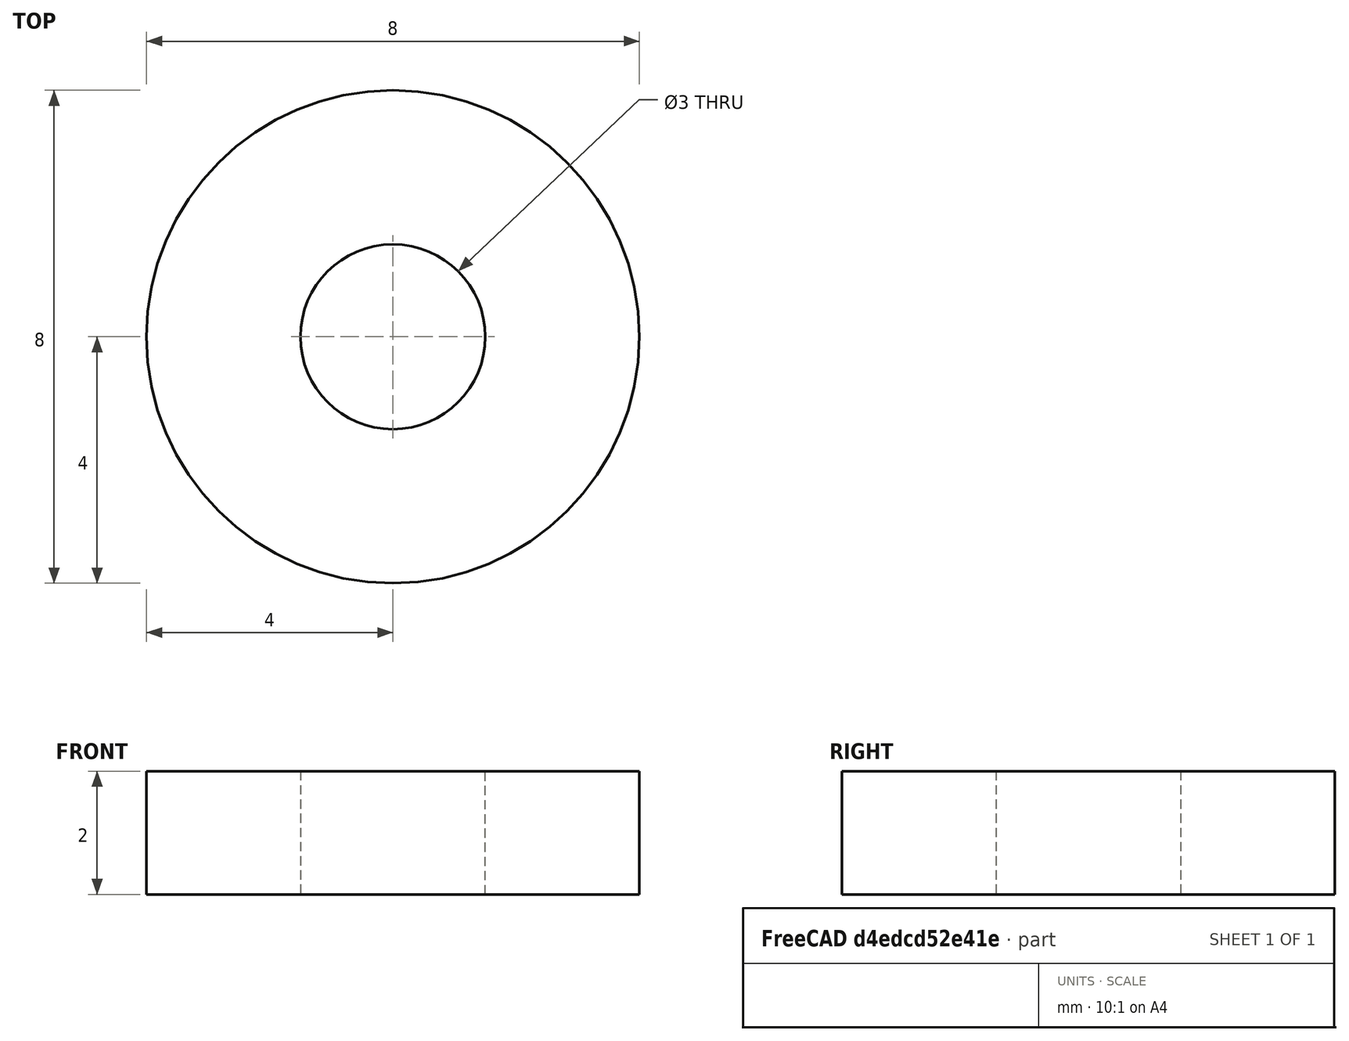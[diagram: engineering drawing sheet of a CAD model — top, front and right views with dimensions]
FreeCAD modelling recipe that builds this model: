
FCSTD DOCUMENT  (FreeCAD 0.19R24276 (Git))
Label: M3_gaika_1
License: All rights reserved
LicenseURL: http://en.wikipedia.org/wiki/All_rights_reserved
objects: Sketcher::SketchObject×1, PartDesign::Pad×1, PartDesign::Body×1
note: 4 computed .brp shape members not serialized (recipe doc carries the construction recipe); baked Part::Feature solids carry a one-line shape summary decoded from their .brp

FEATURE [Sketcher::SketchObject] Sketch
  FullyConstrained = true
  MapMode = 5
  Support = -> [XY_Plane]
  sketch-geometry (2):
    g0: Circle CenterX=0 CenterY=0 CenterZ=0 NormalX=0 NormalY=0 NormalZ=1 AngleXU=0 Radius=4
    g1: Circle CenterX=0 CenterY=0 CenterZ=0 NormalX=0 NormalY=0 NormalZ=1 AngleXU=0 Radius=1.5
  constraints (4):
    c: Coincident(g0,g-1)
    c: Coincident(g1,g0)
    c: Diameter(g1) = 3
    c: Diameter(g0) = 8
FEATURE [PartDesign::Pad] Pad
  Direction = (1,1,1)
  Length = 2
  Length2 = 100
  Profile = -> Sketch
  Type = 0
FEATURE [PartDesign::Body] Body
  Group = -> [Sketch,Pad]
  Origin = -> Origin
  Tip = -> Pad
